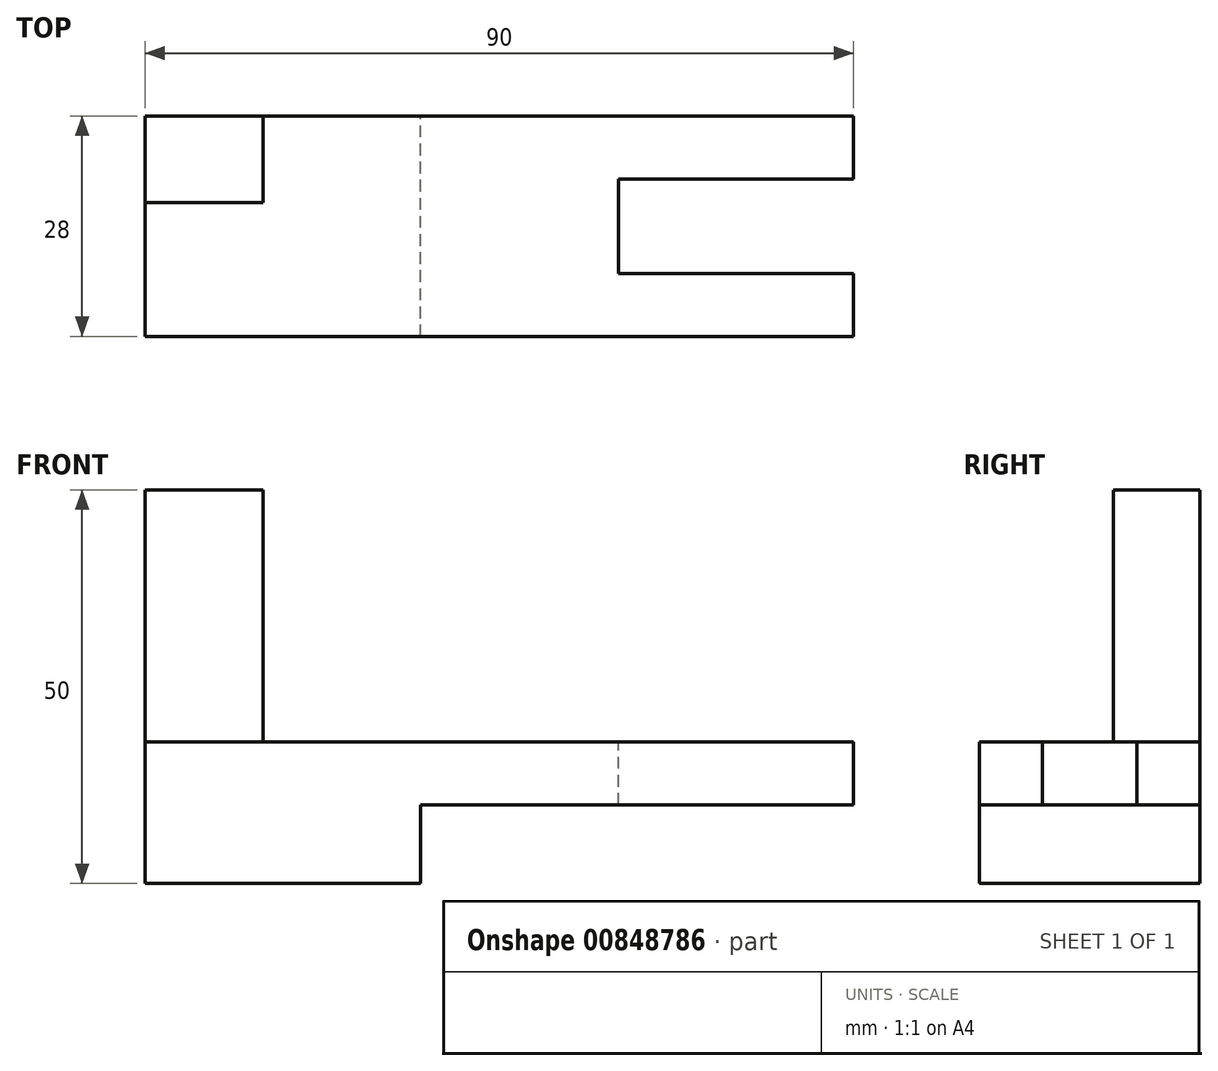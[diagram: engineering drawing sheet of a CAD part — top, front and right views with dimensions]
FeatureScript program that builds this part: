
annotation { "Feature Type Name" : "Feature", "Feature Type Description" : "" }
export const myFeature = defineFeature(function(context is Context, id is Id, definition is map)
    precondition{}
    {
        {
            var Q0;
            Q0=qCreatedBy(makeId("Front.planeOp"),FACE);
            var sketch = newSketch(context, id + "F0", { "sketchPlane" : qUnion([Q0])});
            skLineSegment(sketch, "E0", {"start": v(0, 0) * mm, "end": v(35, 0) * mm});
            skLineSegment(sketch, "E1", {"start": v(35, 0) * mm, "end": v(35, 10) * mm});
            skLineSegment(sketch, "E2", {"start": v(35, 10) * mm, "end": v(90, 10) * mm});
            skLineSegment(sketch, "E3", {"start": v(90, 10) * mm, "end": v(90, 18) * mm});
            skLineSegment(sketch, "E4", {"start": v(90, 18) * mm, "end": v(15, 18) * mm});
            skLineSegment(sketch, "E5", {"start": v(15, 18) * mm, "end": v(15, 50) * mm});
            skLineSegment(sketch, "E6", {"start": v(15, 50) * mm, "end": v(0, 50) * mm});
            skLineSegment(sketch, "E7", {"start": v(0, 50) * mm, "end": v(0, 0) * mm});
            skSolve(sketch);
        }
        {
            var Q0;
            Q0 = qSketchRegion(id + "F0", true);
            extrude(context, id + "F1", {"entities" : qUnion([Q0]), "depth" : 28 * mm, "offsetDistance" : 25 * mm});
        }
        {
            var Q0;
            Q0=makeQuery(id+"F1.opExtrude","SWEPT_FACE",FACE,{"disambiguationData":[OSD([sQuery(id+"F0.wireOp",EDGE,"E5")])]});
            var sketch = newSketch(context, id + "F2", { "sketchPlane" : qUnion([Q0])});
            skLineSegment(sketch, "E8", {"start": v(-28, 18) * mm, "end": v(-11, 18) * mm});
            skLineSegment(sketch, "E9", {"start": v(-11, 18) * mm, "end": v(-11, 50) * mm});
            skSolve(sketch);
        }
        {
            var Q0;
            Q0=makeQuery(id+"F2.imprint","IMPRINT",FACE,{"disambiguationData":[TD([[makeQuery(id+"F2.imprint","IMPRINT",EDGE,{"derivedFrom":sQuery(id+"F2.wireOp",EDGE,"E8")}),1.0]])]});
            extrude(context, id + "F3", {"entities" : qUnion([Q0]), "operationType" : NewBodyOperationType.REMOVE, "oppositeDirection" : true, "depth" : 25 * mm, "offsetDistance" : 25 * mm});
        }
        {
            var Q0;
            Q0=makeQuery(id+"F3.boolean.opBoolean","MERGE",FACE,{"derivedFrom":[makeQuery(id+"F1.opExtrude","SWEPT_FACE",FACE,{"disambiguationData":[OSD([sQuery(id+"F0.wireOp",EDGE,"E4")])]}),makeQuery(id+"F3.opExtrude","SWEPT_FACE",FACE,{"disambiguationData":[OSD([sQuery(id+"F2.wireOp",EDGE,"E8")])]})]});
            var sketch = newSketch(context, id + "F4", { "sketchPlane" : qUnion([Q0])});
            skLineSegment(sketch, "E10", {"start": v(60.14, -8) * mm, "end": v(90, -8) * mm});
            skLineSegment(sketch, "E11", {"start": v(90, -20) * mm, "end": v(60.14, -20) * mm});
            skLineSegment(sketch, "E12", {"start": v(60.14, -20) * mm, "end": v(60.14, -8) * mm});
            skSolve(sketch);
        }
        {
            var Q0;
            {var subQ0=sQuery(id+"F4.wireOp",EDGE,"E10");Q0=makeQuery(id+"F4.imprint","IMPRINT",FACE,{"disambiguationData":[TD([[makeQuery(id+"F4.imprint","IMPRINT",EDGE,{"derivedFrom":subQ0}),-1.0]])]});}
            extrude(context, id + "F5", {"entities" : qUnion([Q0]), "operationType" : NewBodyOperationType.REMOVE, "oppositeDirection" : true, "depth" : 25 * mm, "offsetDistance" : 25 * mm});
        }
    });
